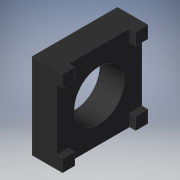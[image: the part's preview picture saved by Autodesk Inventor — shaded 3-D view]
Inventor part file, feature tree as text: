
AUTODESK INVENTOR PART (.ipt)
format: ipt  version: 2019 (Build 230136000, 136)  size: 128,512 bytes
history: native  units: mm
features: other x7, extrude x2, sketch x2
ambient origin geometry x8: Origin, YZ Plane, XZ Plane, XY Plane, X Axis, Y Axis, Z Axis, Center Point
bodies: Solid1 (feature_tree)
feature tree (11):
  extrude  "Extrusion1"  Depth=1.0mm TaperAngle=0.0deg
  extrude  "Extrusion2"  [1 undecoded]
  other  "GUS_4502_1_XY"
  other  "GUS_4502_1_YZ"
  other  "GUS_4502_1_ZX"
  other  "GUS_4502_1_X"
  other  "GUS_4502_1_Y"
  other  "GUS_4502_1_Z"
  other  "GUS_4502_1_Center"
  sketch  "Skizze_1"  dims[d0=5.0mm d1=0.0mm d2=1.0mm d3=0.0mm]
  sketch  "Skizze_2"  dims[d4=0.0mm]
note: 1 required parameter value undecoded (feature->parameter linkage not recoverable at this tier; creation-order binding heuristic only, values carry confidence <= 0.55)
